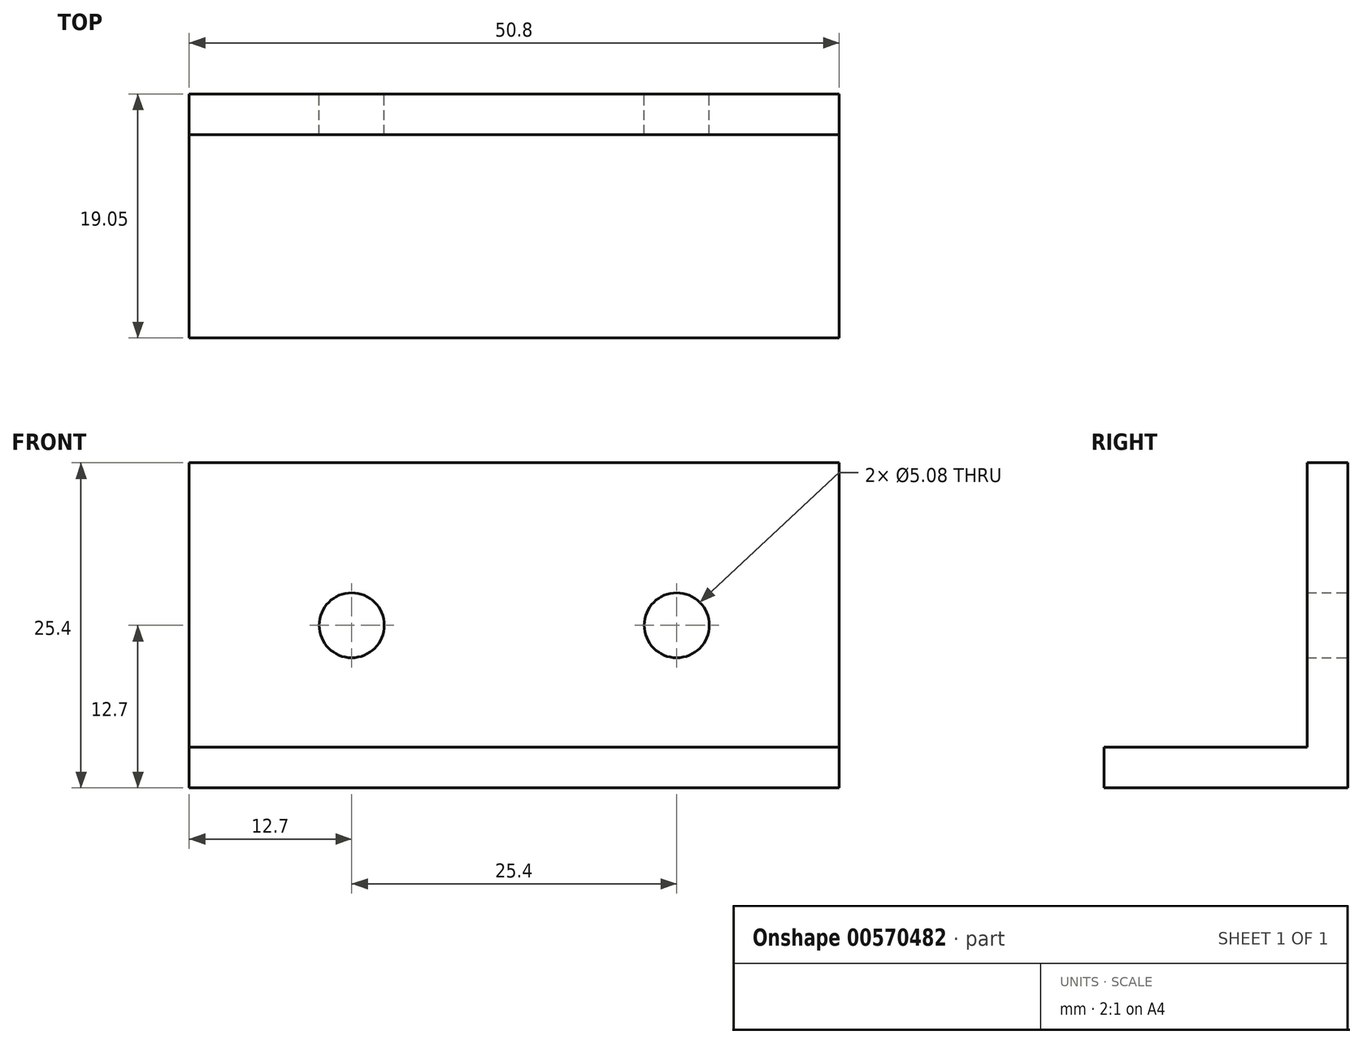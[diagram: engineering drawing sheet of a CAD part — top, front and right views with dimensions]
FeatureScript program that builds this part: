
annotation { "Feature Type Name" : "Feature", "Feature Type Description" : "" }
export const myFeature = defineFeature(function(context is Context, id is Id, definition is map)
    precondition{}
    {
        {
            var Q0;
            Q0=qCreatedBy(makeId("Right.planeOp"),FACE);
            var sketch = newSketch(context, id + "F0", { "sketchPlane" : qUnion([Q0])});
            skLineSegment(sketch, "E0.bottom", {"start": v(0, 0) * mm, "end": v(-19.05, 0) * mm});
            skLineSegment(sketch, "E0.top", {"start": v(0, 25.4) * mm, "end": v(-3.18, 25.4) * mm});
            skLineSegment(sketch, "E0.left", {"start": v(0, 0) * mm, "end": v(0, 25.4) * mm});
            skLineSegment(sketch, "E0.right", {"start": v(-19.05, 0) * mm, "end": v(-19.05, 3.18) * mm});
            skLineSegment(sketch, "E1.top", {"start": v(-19.05, 3.18) * mm, "end": v(-3.17, 3.18) * mm});
            skLineSegment(sketch, "E1.right", {"start": v(-3.18, 25.4) * mm, "end": v(-3.17, 3.18) * mm});
            skSolve(sketch);
        }
        {
            var Q0;
            Q0 = qSketchRegion(id + "F0", true);
            extrude(context, id + "F1", {"entities" : qUnion([Q0]), "depth" : 50.8 * mm, "offsetDistance" : 25.4 * mm});
        }
        {
            var Q0;
            Q0=qCreatedBy(makeId("Front.planeOp"),FACE);
            var sketch = newSketch(context, id + "F2", { "sketchPlane" : qUnion([Q0])});
            skCircle(sketch, "E2", {"center": v(38.1, 12.7) * mm, "radius": 2.54 * mm});
            skCircle(sketch, "E3", {"center": v(12.7, 12.7) * mm, "radius": 2.54 * mm});
            skSolve(sketch);
        }
        {
            var Q0;
            Q0 = qSketchRegion(id + "F2", true);
            extrude(context, id + "F3", {"entities" : qUnion([Q0]), "operationType" : NewBodyOperationType.REMOVE, "depth" : 25.4 * mm, "offsetDistance" : 25.4 * mm});
        }
    });
